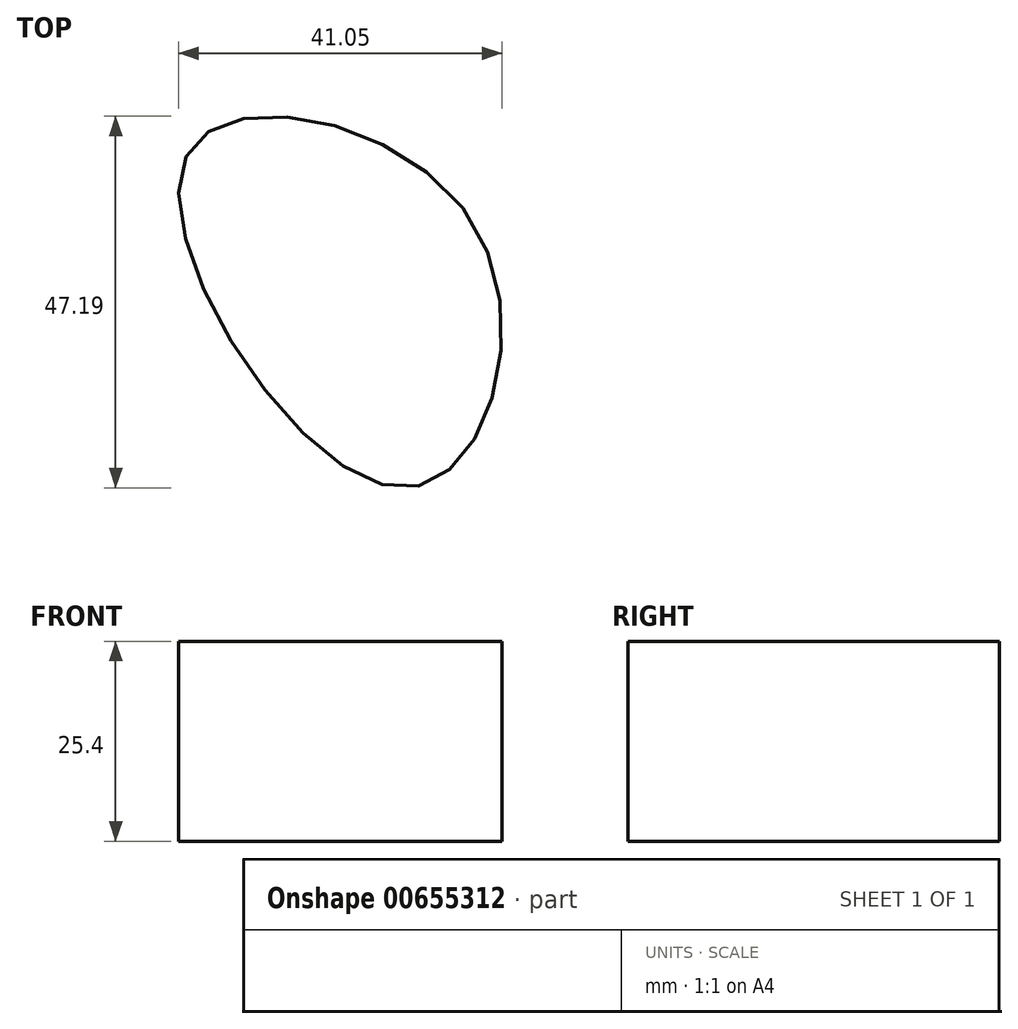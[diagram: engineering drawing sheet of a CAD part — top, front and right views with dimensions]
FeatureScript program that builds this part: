
annotation { "Feature Type Name" : "Feature", "Feature Type Description" : "" }
export const myFeature = defineFeature(function(context is Context, id is Id, definition is map)
    precondition{}
    {
        {
            var Q0;
            Q0=qCreatedBy(makeId("Top.planeOp"),FACE);
            var sketch = newSketch(context, id + "F0", { "sketchPlane" : qUnion([Q0])});
            skFitSpline(sketch, "E0", {"points": [v(-60.72, 8.56) * mm, v(-33.3, -33.54) * mm, v(-24.2, 0) * mm, v(-60.72, 8.56) * mm]});
            skSolve(sketch);
        }
        {
            var Q0;
            Q0=makeQuery(id+"F0.imprint","IMPRINT",FACE,{"disambiguationData":[TD([[makeQuery(id+"F0.imprint","IMPRINT",EDGE,{"derivedFrom":sQuery(id+"F0.wireOp",EDGE,"E0")}),1.0]])]});
            extrude(context, id + "F1", {"entities" : qUnion([Q0]), "depth" : 25.4 * mm, "offsetDistance" : 25.4 * mm});
        }
    });
